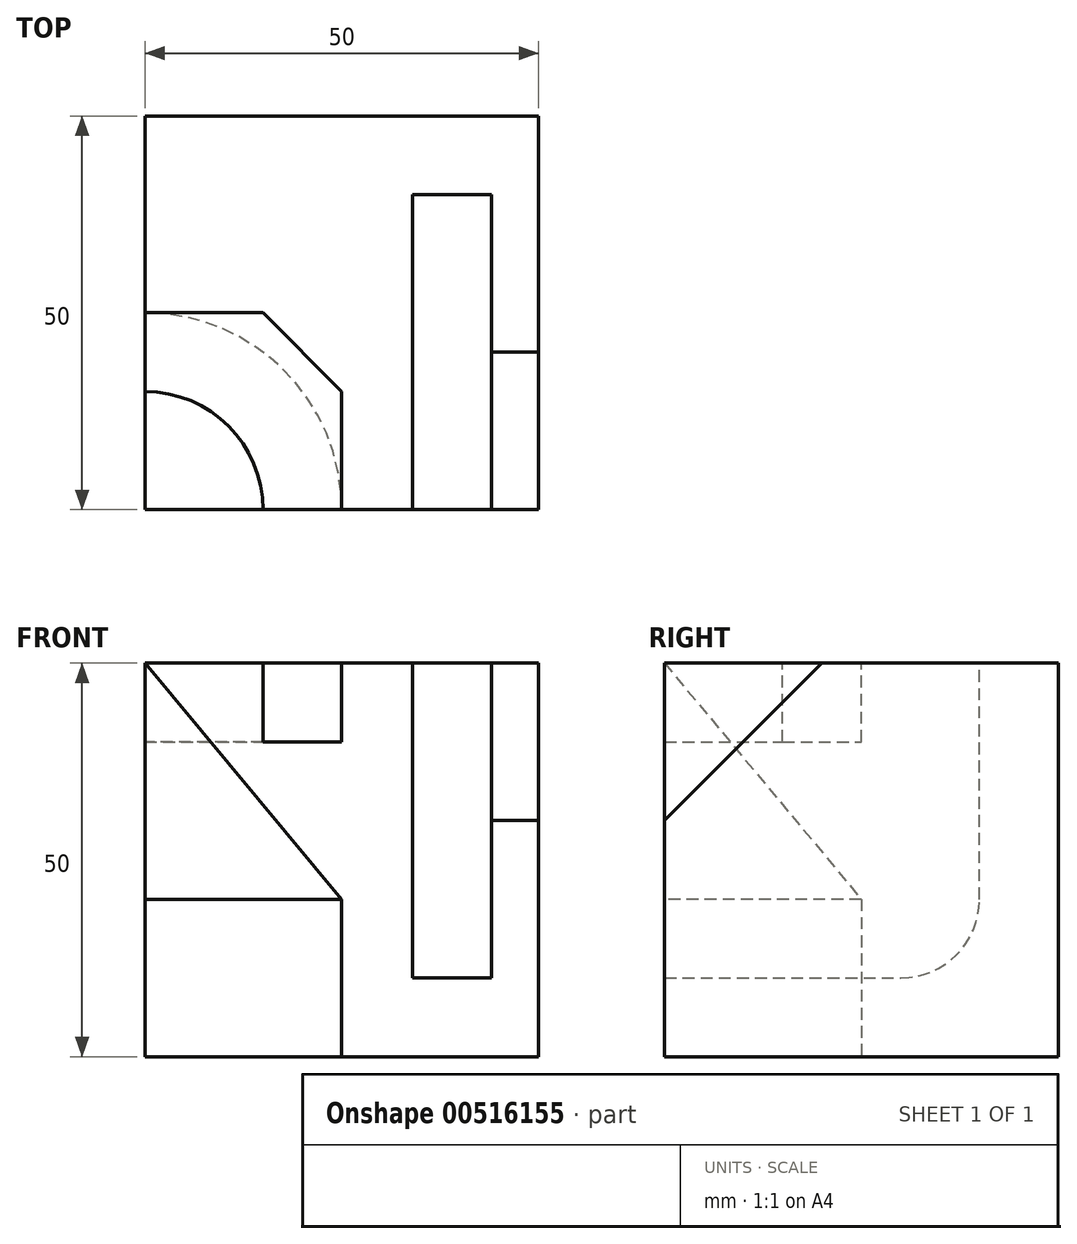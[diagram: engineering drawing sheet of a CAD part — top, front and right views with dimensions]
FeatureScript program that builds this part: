
annotation { "Feature Type Name" : "Feature", "Feature Type Description" : "" }
export const myFeature = defineFeature(function(context is Context, id is Id, definition is map)
    precondition{}
    {
        {
            var Q0;
            Q0=qCreatedBy(makeId("Top.planeOp"),FACE);
            var sketch = newSketch(context, id + "F0", { "sketchPlane" : qUnion([Q0])});
            skLineSegment(sketch, "E0.bottom", {"start": v(0, 0) * mm, "end": v(50, 0) * mm});
            skLineSegment(sketch, "E0.top", {"start": v(0, 50) * mm, "end": v(50, 50) * mm});
            skLineSegment(sketch, "E0.left", {"start": v(0, 0) * mm, "end": v(0, 50) * mm});
            skLineSegment(sketch, "E0.right", {"start": v(50, 0) * mm, "end": v(50, 50) * mm});
            skSolve(sketch);
        }
        {
            var Q0;
            Q0=makeQuery(id+"F0.imprint","IMPRINT",FACE,{"disambiguationData":[TD([[makeQuery(id+"F0.imprint","IMPRINT",EDGE,{"derivedFrom":sQuery(id+"F0.wireOp",EDGE,"E0.bottom")}),1.0]])]});
            extrude(context, id + "F1", {"entities" : qUnion([Q0]), "depth" : 50 * mm, "offsetDistance" : 25 * mm});
        }
        {
            var Q0;
            Q0=makeQuery(id+"F1.opExtrude","CAP_FACE",FACE,{"disambiguationData":[OSD([sQuery(id+"F0.wireOp",EDGE,"E0.bottom"),sQuery(id+"F0.wireOp",EDGE,"E0.top"),sQuery(id+"F0.wireOp",EDGE,"E0.left"),sQuery(id+"F0.wireOp",EDGE,"E0.right")])],"isStart":false});
            var sketch = newSketch(context, id + "F2", { "sketchPlane" : qUnion([Q0])});
            skLineSegment(sketch, "E1", {"start": v(44, 0) * mm, "end": v(44, 40) * mm});
            skLineSegment(sketch, "E2", {"start": v(44, 40) * mm, "end": v(34, 40) * mm});
            skLineSegment(sketch, "E3", {"start": v(34, 40) * mm, "end": v(34, 0) * mm});
            skSolve(sketch);
        }
        {
            var Q0;
            {var subQ0=sQuery(id+"F2.wireOp",EDGE,"E1");Q0=makeQuery(id+"F2.imprint","IMPRINT",FACE,{"disambiguationData":[TD([[makeQuery(id+"F2.imprint","IMPRINT",EDGE,{"derivedFrom":subQ0}),1.0]])]});}
            extrude(context, id + "F3", {"entities" : qUnion([Q0]), "operationType" : NewBodyOperationType.REMOVE, "oppositeDirection" : true, "depth" : 40 * mm, "offsetDistance" : 25 * mm});
        }
        {
            var Q0;
            Q0=makeQuery(id+"F1.opExtrude","CAP_FACE",FACE,{"disambiguationData":[OSD([sQuery(id+"F0.wireOp",EDGE,"E0.bottom"),sQuery(id+"F0.wireOp",EDGE,"E0.top"),sQuery(id+"F0.wireOp",EDGE,"E0.left"),sQuery(id+"F0.wireOp",EDGE,"E0.right")])],"isStart":true});
            var sketch = newSketch(context, id + "F4", { "sketchPlane" : qUnion([Q0])});
            skCircle(sketch, "E4", {"center": v(0, 0) * mm, "radius": 25 * mm});
            skSolve(sketch);
        }
        {
            var Q0;
            {var subQ0=sQuery(id+"F4.wireOp",EDGE,"E4");var subQ1=makeQuery(id+"F1.opExtrude","CAP_EDGE",EDGE,{"disambiguationData":[OSD([sQuery(id+"F0.wireOp",EDGE,"E0.bottom")])],"isStart":true});var subQ2=makeQuery(id+"F4.imprint","INTERSECT",VERTEX,{"derivedFrom":[subQ1,subQ0]});Q0=makeQuery(id+"F4.imprint","IMPRINT",FACE,{"disambiguationData":[TD([[makeQuery(id+"F4.imprint","IMPRINT",EDGE,{"disambiguationData":[TD([[subQ2,1.0]])],"derivedFrom":subQ0}),1.0]])]});}
            extrude(context, id + "F5", {"entities" : qUnion([Q0]), "operationType" : NewBodyOperationType.REMOVE, "oppositeDirection" : true, "depth" : 20 * mm, "offsetDistance" : 25 * mm});
        }
        {
            var Q0;
            Q0=makeQuery(id+"F1.opExtrude","CAP_FACE",FACE,{"disambiguationData":[OSD([sQuery(id+"F0.wireOp",EDGE,"E0.bottom"),sQuery(id+"F0.wireOp",EDGE,"E0.top"),sQuery(id+"F0.wireOp",EDGE,"E0.left"),sQuery(id+"F0.wireOp",EDGE,"E0.right")])],"isStart":false});
            var sketch = newSketch(context, id + "F6", { "sketchPlane" : qUnion([Q0])});
            skLineSegment(sketch, "E5", {"start": v(50, 20) * mm, "end": v(44, 20) * mm});
            skSolve(sketch);
        }
        {
            var Q0;
            Q0=makeQuery(id+"F1.opExtrude","SWEPT_FACE",FACE,{"disambiguationData":[OSD([sQuery(id+"F0.wireOp",EDGE,"E0.bottom")])]});
            var sketch = newSketch(context, id + "F7", { "sketchPlane" : qUnion([Q0])});
            skLineSegment(sketch, "E6", {"start": v(0, 50) * mm, "end": v(0, 20) * mm});
            skLineSegment(sketch, "E7", {"start": v(0, 20) * mm, "end": v(25, 20) * mm});
            skLineSegment(sketch, "E8", {"start": v(25, 20) * mm, "end": v(0, 50) * mm});
            skSolve(sketch);
        }
        {
            var Q0;
            Q0=makeQuery(id+"F7.imprint","IMPRINT",FACE,{"disambiguationData":[TD([[makeQuery(id+"F7.imprint","IMPRINT",EDGE,{"derivedFrom":sQuery(id+"F7.wireOp",EDGE,"E6")}),1.0]])]});
            var Q1;
            Q1=sQuery(id+"F7.wireOp",EDGE,"E6");
            revolve(context, id + "F8", {"operationType" : NewBodyOperationType.REMOVE, "entities" : qUnion([Q0]), "axis" : qUnion([Q1]), "revolveType" : RevolveType.FULL, "oppositeDirection" : true});
        }
        {
            var Q0;
            Q0=makeQuery(id+"F1.opExtrude","SWEPT_FACE",FACE,{"disambiguationData":[OSD([sQuery(id+"F0.wireOp",EDGE,"E0.right")])]});
            var sketch = newSketch(context, id + "F9", { "sketchPlane" : qUnion([Q0])});
            skLineSegment(sketch, "E9", {"start": v(20, 50) * mm, "end": v(0, 30) * mm});
            skSolve(sketch);
        }
        {
            var Q0;
            {var subQ0=sQuery(id+"F6.wireOp",EDGE,"E5");Q0=makeQuery(id+"F6.imprint","IMPRINT",FACE,{"disambiguationData":[TD([[makeQuery(id+"F6.imprint","IMPRINT",EDGE,{"derivedFrom":subQ0}),1.0]])]});}
            var Q1;
            Q1=sQuery(id+"F9.wireOp",EDGE,"E9");
            sweep(context, id + "F10", {"operationType" : NewBodyOperationType.REMOVE, "profiles" : qUnion([Q0]), "path" : qUnion([Q1])});
        }
        {
            var Q0;
            Q0=makeQuery(id+"F3.boolean.opBoolean","COPY",EDGE,{"derivedFrom":makeQuery(id+"F3.opExtrude","CAP_EDGE",EDGE,{"disambiguationData":[OSD([sQuery(id+"F2.wireOp",EDGE,"E2")])],"isStart":false})});
            fillet(context, id + "F11", {"entities" : qUnion([Q0]), "radius" : 10 * mm, "tangentPropagation" : true, "allowEdgeOverflow" : false});
        }
        {
            var Q0;
            Q0=makeQuery(id+"F1.opExtrude","CAP_FACE",FACE,{"disambiguationData":[OSD([sQuery(id+"F0.wireOp",EDGE,"E0.bottom"),sQuery(id+"F0.wireOp",EDGE,"E0.top"),sQuery(id+"F0.wireOp",EDGE,"E0.left"),sQuery(id+"F0.wireOp",EDGE,"E0.right")])],"isStart":false});
            var sketch = newSketch(context, id + "F12", { "sketchPlane" : qUnion([Q0])});
            skCircle(sketch, "E10", {"center": v(0, 0) * mm, "radius": 15 * mm});
            skLineSegment(sketch, "E11.bottom", {"start": v(0, 0) * mm, "end": v(25, 0) * mm});
            skLineSegment(sketch, "E11.top", {"start": v(0, 25) * mm, "end": v(25, 25) * mm});
            skLineSegment(sketch, "E11.left", {"start": v(0, 0) * mm, "end": v(0, 25) * mm});
            skLineSegment(sketch, "E11.right", {"start": v(25, 0) * mm, "end": v(25, 25) * mm});
            skSolve(sketch);
        }
        {
            var Q0;
            {var subQ1=sQuery(id+"F12.wireOp",EDGE,"E11.top");Q0=makeQuery(id+"F12.imprint","IMPRINT",FACE,{"disambiguationData":[TD([[makeQuery(id+"F12.imprint","IMPRINT",EDGE,{"derivedFrom":subQ1}),-1.0]])]});}
            extrude(context, id + "F13", {"entities" : qUnion([Q0]), "operationType" : NewBodyOperationType.REMOVE, "oppositeDirection" : true, "depth" : 10 * mm, "offsetDistance" : 25 * mm});
        }
        {
            var Q0;
            Q0=makeQuery(id+"F13.boolean.opBoolean","COPY",EDGE,{"derivedFrom":makeQuery(id+"F13.opExtrude","SWEPT_EDGE",EDGE,{"disambiguationData":[OSD([sQuery(id+"F12.wireOp",EDGE,"E11.top"),sQuery(id+"F12.wireOp",EDGE,"E11.right")])]})});
            chamfer(context, id + "F14", {"entities" : qUnion([Q0]), "width" : 10 * mm, "tangentPropagation" : true});
        }
    });
